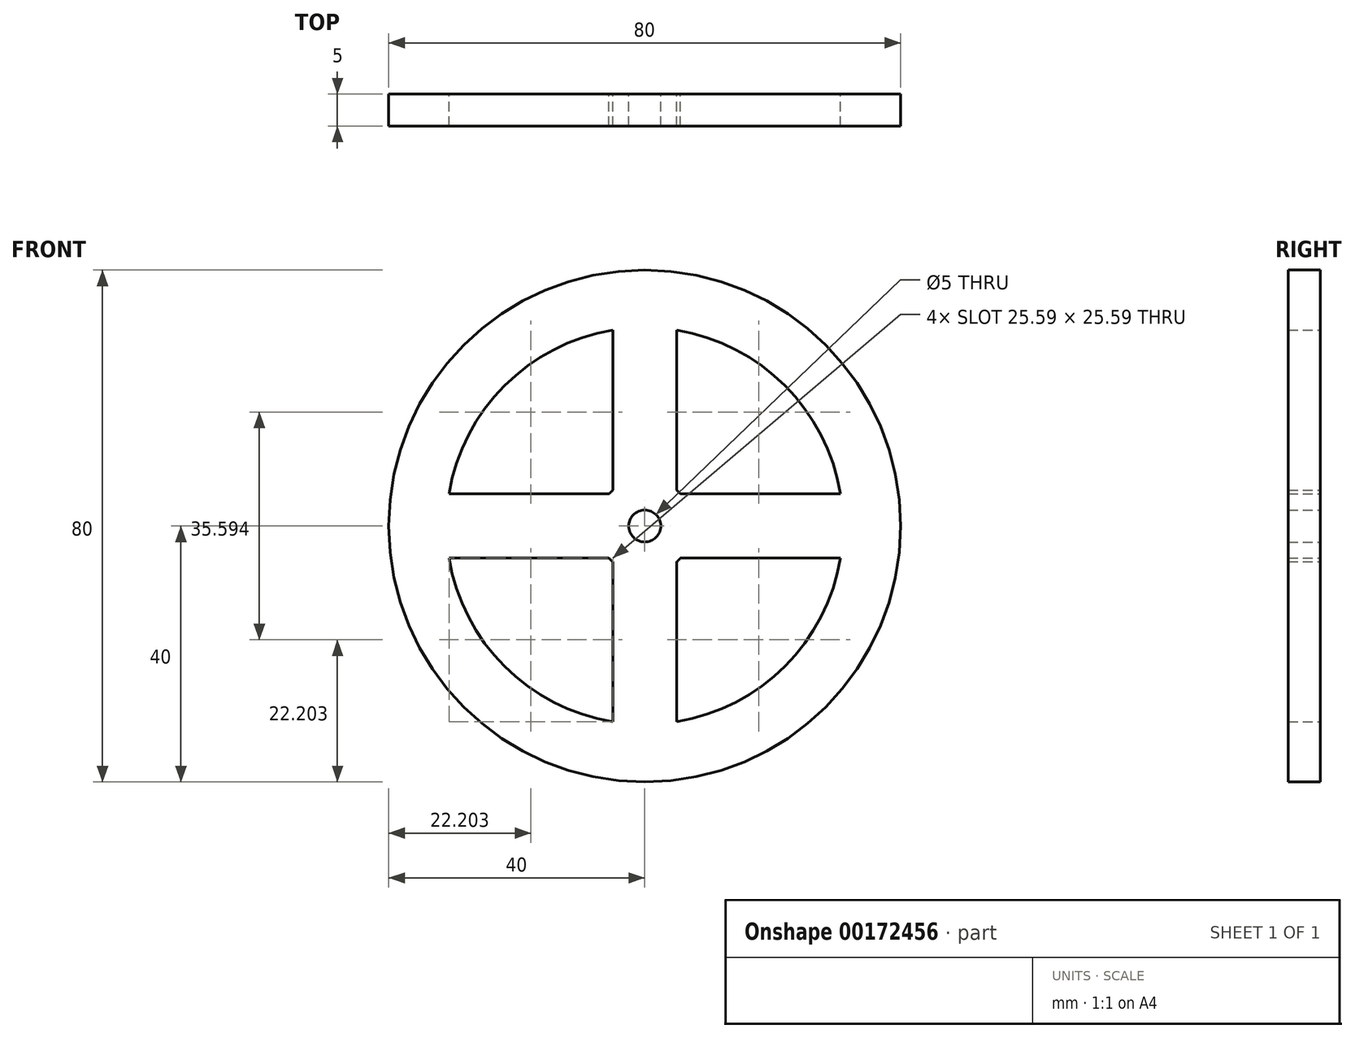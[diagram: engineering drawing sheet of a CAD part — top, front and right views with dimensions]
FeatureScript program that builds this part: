
annotation { "Feature Type Name" : "Feature", "Feature Type Description" : "" }
export const myFeature = defineFeature(function(context is Context, id is Id, definition is map)
    precondition{}
    {
        {
            var Q0;
            Q0=qCreatedBy(makeId("Front.planeOp"),FACE);
            var sketch = newSketch(context, id + "F0", { "sketchPlane" : qUnion([Q0])});
            skCircle(sketch, "E0", {"center": v(0, 0) * mm, "radius": 40 * mm});
            skArc(sketch, "E1", {"start": v(-5, 30.6) * mm, "mid": v(-21.92, 21.92) * mm, "end": v(-30.6, 5) * mm});
            skArc(sketch, "E2", {"start": v(-5, 5.6) * mm, "mid": v(-5.3, 5.3) * mm, "end": v(-5.6, 5) * mm});
            skLineSegment(sketch, "E3", {"start": v(0, 0) * mm, "end": v(0, 31) * mm, "construction": true});
            skLineSegment(sketch, "E4", {"start": v(0, 0) * mm, "end": v(31, 0) * mm, "construction": true});
            skLineSegment(sketch, "E5", {"start": v(0, 0) * mm, "end": v(0, -31) * mm, "construction": true});
            skLineSegment(sketch, "E6", {"start": v(0, 0) * mm, "end": v(-31, 0) * mm, "construction": true});
            skCircle(sketch, "E7", {"center": v(0, 0) * mm, "radius": 2.5 * mm});
            skLineSegment(sketch, "E8.0", {"start": v(-5.6, -5) * mm, "end": v(-30.6, -5) * mm});
            skLineSegment(sketch, "E9.0", {"start": v(5, -5.6) * mm, "end": v(5, -30.6) * mm});
            skLineSegment(sketch, "E10.0", {"start": v(-5, -5.6) * mm, "end": v(-5, -30.6) * mm});
            skLineSegment(sketch, "E11.0", {"start": v(5.6, -5) * mm, "end": v(30.6, -5) * mm});
            skLineSegment(sketch, "E12.0", {"start": v(5.6, 5) * mm, "end": v(30.6, 5) * mm});
            skLineSegment(sketch, "E13.trimOffspring", {"start": v(-5, 5.6) * mm, "end": v(-5, 30.6) * mm});
            skLineSegment(sketch, "E14.trimOffspring", {"start": v(-5.6, 5) * mm, "end": v(-30.6, 5) * mm});
            skLineSegment(sketch, "E15.trimOffspring", {"start": v(5, 5.6) * mm, "end": v(5, 30.6) * mm});
            skArc(sketch, "E16.trimOffspring", {"start": v(5.6, 5) * mm, "mid": v(5.3, 5.3) * mm, "end": v(5, 5.6) * mm});
            skArc(sketch, "E17.trimOffspring", {"start": v(5, -5.6) * mm, "mid": v(5.3, -5.3) * mm, "end": v(5.6, -5) * mm});
            skArc(sketch, "E18.trimOffspring", {"start": v(-5.6, -5) * mm, "mid": v(-5.3, -5.3) * mm, "end": v(-5, -5.6) * mm});
            skArc(sketch, "E19.trimOffspring", {"start": v(30.6, 5) * mm, "mid": v(21.92, 21.92) * mm, "end": v(5, 30.6) * mm});
            skArc(sketch, "E20.trimOffspring", {"start": v(5, -30.6) * mm, "mid": v(21.92, -21.92) * mm, "end": v(30.6, -5) * mm});
            skArc(sketch, "E21.trimOffspring", {"start": v(-30.6, -5) * mm, "mid": v(-21.92, -21.92) * mm, "end": v(-5, -30.6) * mm});
            skSolve(sketch);
        }
        {
            var Q0;
            Q0 = qSketchRegion(id + "F0", true);
            extrude(context, id + "F1", {"entities" : qUnion([Q0]), "depth" : 5 * mm});
        }
    });
